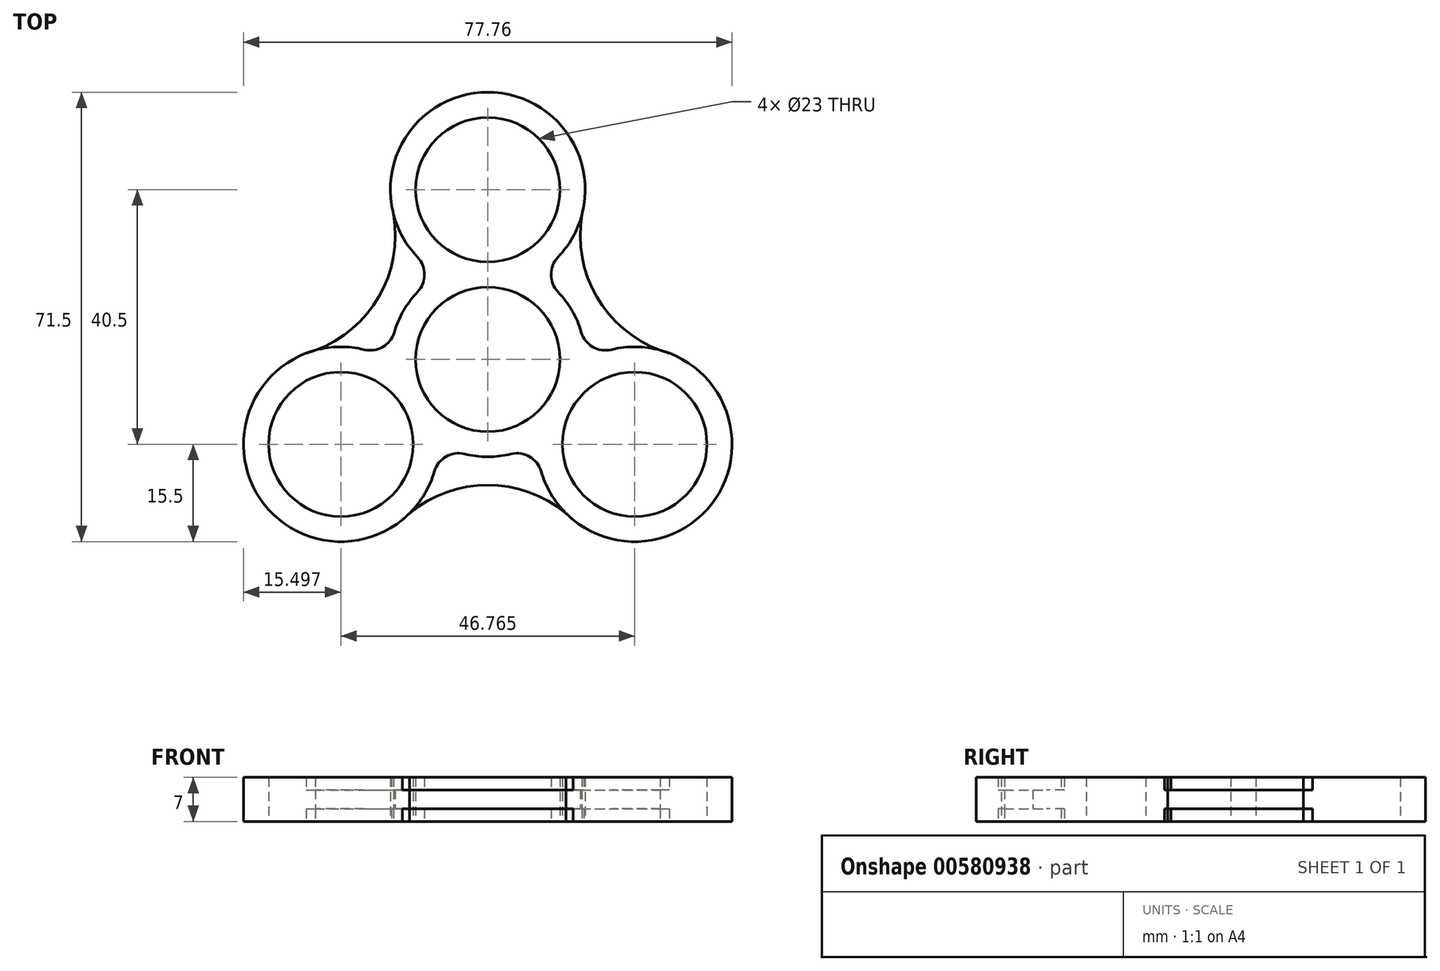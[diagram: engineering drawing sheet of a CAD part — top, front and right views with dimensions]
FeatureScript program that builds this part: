
annotation { "Feature Type Name" : "Feature", "Feature Type Description" : "" }
export const myFeature = defineFeature(function(context is Context, id is Id, definition is map)
    precondition{}
    {
        {
            var Q0;
            Q0=qCreatedBy(makeId("Top.planeOp"),FACE);
            var sketch = newSketch(context, id + "F0", { "sketchPlane" : qUnion([Q0])});
            skCircle(sketch, "E0", {"center": v(0, 0) * mm, "radius": 11.5 * mm});
            skLineSegment(sketch, "E1", {"start": v(0, 0) * mm, "end": v(0, 27) * mm});
            skCircle(sketch, "E2", {"center": v(0, 27) * mm, "radius": 11.5 * mm});
            skArc(sketch, "E3.0", {"start": v(11.18, 16.27) * mm, "mid": v(0, 42.5) * mm, "end": v(-11.18, 16.27) * mm});
            skCircle(sketch, "E4.1.0", {"center": v(-23.38, -13.5) * mm, "radius": 11.5 * mm});
            skArc(sketch, "E4.1.1", {"start": v(-19.68, 1.55) * mm, "mid": v(-36.8, -21.25) * mm, "end": v(-8.5, -17.82) * mm});
            skCircle(sketch, "E4.2.0", {"center": v(23.38, -13.5) * mm, "radius": 11.5 * mm});
            skArc(sketch, "E4.2.1", {"start": v(8.5, -17.82) * mm, "mid": v(36.8, -21.25) * mm, "end": v(19.68, 1.55) * mm});
            skArc(sketch, "E5", {"start": v(15.3, 24.5) * mm, "mid": v(17.31, 10) * mm, "end": v(28.87, 1) * mm});
            skArc(sketch, "E6.0", {"start": v(-11.18, 10.73) * mm, "mid": v(-13.42, 7.75) * mm, "end": v(-14.89, 4.32) * mm});
            skArc(sketch, "E7.trimOffspring", {"start": v(14.89, 4.32) * mm, "mid": v(13.42, 7.75) * mm, "end": v(11.18, 10.73) * mm});
            skArc(sketch, "E8.trimOffspring", {"start": v(-3.7, -15.05) * mm, "mid": v(0, -15.5) * mm, "end": v(3.7, -15.05) * mm});
            skPoint(sketch, "E9.visualSharp", {"position": v(7.62, 13.5) * mm});
            skArc(sketch, "E9.filletArc", {"start": v(11.18, 16.27) * mm, "mid": v(10.07, 13.5) * mm, "end": v(11.18, 10.73) * mm});
            skPoint(sketch, "E10.visualSharp", {"position": v(15.5, -0.15) * mm});
            skArc(sketch, "E10.filletArc", {"start": v(14.89, 4.32) * mm, "mid": v(16.73, 1.97) * mm, "end": v(19.68, 1.55) * mm});
            skPoint(sketch, "E11.visualSharp", {"position": v(7.88, -13.35) * mm});
            skArc(sketch, "E11.filletArc", {"start": v(8.5, -17.82) * mm, "mid": v(6.66, -15.47) * mm, "end": v(3.7, -15.05) * mm});
            skPoint(sketch, "E12.visualSharp", {"position": v(-7.88, -13.35) * mm});
            skArc(sketch, "E12.filletArc", {"start": v(-3.7, -15.05) * mm, "mid": v(-6.66, -15.47) * mm, "end": v(-8.5, -17.82) * mm});
            skPoint(sketch, "E13.visualSharp", {"position": v(-15.5, -0.15) * mm});
            skArc(sketch, "E13.filletArc", {"start": v(-19.68, 1.55) * mm, "mid": v(-16.73, 1.97) * mm, "end": v(-14.89, 4.32) * mm});
            skPoint(sketch, "E14.visualSharp", {"position": v(-7.62, 13.5) * mm});
            skArc(sketch, "E14.filletArc", {"start": v(-11.18, 10.73) * mm, "mid": v(-10.07, 13.5) * mm, "end": v(-11.18, 16.27) * mm});
            skArc(sketch, "E15.1.0", {"start": v(-28.87, 1) * mm, "mid": v(-17.31, 10) * mm, "end": v(-15.3, 24.5) * mm});
            skArc(sketch, "E15.2.0", {"start": v(13.57, -25.5) * mm, "mid": v(0, -20) * mm, "end": v(-13.57, -25.5) * mm});
            skSolve(sketch);
        }
        {
            var Q0;
            Q0=makeQuery(id+"F0.imprint","IMPRINT",FACE,{"disambiguationData":[TD([[makeQuery(id+"F0.imprint","IMPRINT",EDGE,{"derivedFrom":sQuery(id+"F0.wireOp",EDGE,"E0")}),-1.0]])]});
            extrude(context, id + "F1", {"entities" : qUnion([Q0]), "endBound" : BoundingType.SYMMETRIC, "depth" : 7 * mm, "offsetDistance" : 25 * mm});
        }
        {
            var Q0;
            {var subQ0=sQuery(id+"F0.wireOp",EDGE,"E5");var subQ1=sQuery(id+"F0.wireOp",EDGE,"E3.0");var subQ2=makeQuery(id+"F0.imprint","INTERSECT",VERTEX,{"disambiguationData":[OD(0.0)],"derivedFrom":[subQ1,subQ0]});Q0=makeQuery(id+"F0.imprint","IMPRINT",FACE,{"disambiguationData":[TD([[makeQuery(id+"F0.imprint","IMPRINT",EDGE,{"disambiguationData":[TD([[subQ2,1.0]])],"derivedFrom":subQ1}),1.0]])]});}
            var Q1;
            {var subQ0=sQuery(id+"F0.wireOp",EDGE,"E15.1.0");var subQ1=sQuery(id+"F0.wireOp",EDGE,"E3.0");var subQ2=makeQuery(id+"F0.imprint","INTERSECT",VERTEX,{"disambiguationData":[OD(0.0)],"derivedFrom":[subQ1,subQ0]});Q1=makeQuery(id+"F0.imprint","IMPRINT",FACE,{"disambiguationData":[TD([[makeQuery(id+"F0.imprint","IMPRINT",EDGE,{"disambiguationData":[TD([[subQ2,-1.0]])],"derivedFrom":subQ1}),1.0]])]});}
            var Q2;
            {var subQ0=sQuery(id+"F0.wireOp",EDGE,"E15.1.0");var subQ1=sQuery(id+"F0.wireOp",EDGE,"E4.1.1");var subQ2=makeQuery(id+"F0.imprint","INTERSECT",VERTEX,{"disambiguationData":[OD(0.0)],"derivedFrom":[subQ1,subQ0]});Q2=makeQuery(id+"F0.imprint","IMPRINT",FACE,{"disambiguationData":[TD([[makeQuery(id+"F0.imprint","IMPRINT",EDGE,{"disambiguationData":[TD([[subQ2,1.0]])],"derivedFrom":subQ1}),1.0]])]});}
            var Q3;
            {var subQ0=sQuery(id+"F0.wireOp",EDGE,"E15.2.0");var subQ1=sQuery(id+"F0.wireOp",EDGE,"E4.1.1");var subQ2=makeQuery(id+"F0.imprint","INTERSECT",VERTEX,{"disambiguationData":[OD(0.0)],"derivedFrom":[subQ1,subQ0]});Q3=makeQuery(id+"F0.imprint","IMPRINT",FACE,{"disambiguationData":[TD([[makeQuery(id+"F0.imprint","IMPRINT",EDGE,{"disambiguationData":[TD([[subQ2,-1.0]])],"derivedFrom":subQ1}),1.0]])]});}
            var Q4;
            {var subQ0=sQuery(id+"F0.wireOp",EDGE,"E15.2.0");var subQ1=sQuery(id+"F0.wireOp",EDGE,"E4.2.1");var subQ2=makeQuery(id+"F0.imprint","INTERSECT",VERTEX,{"disambiguationData":[OD(0.0)],"derivedFrom":[subQ1,subQ0]});Q4=makeQuery(id+"F0.imprint","IMPRINT",FACE,{"disambiguationData":[TD([[makeQuery(id+"F0.imprint","IMPRINT",EDGE,{"disambiguationData":[TD([[subQ2,1.0]])],"derivedFrom":subQ1}),1.0]])]});}
            var Q5;
            {var subQ0=sQuery(id+"F0.wireOp",EDGE,"E5");var subQ1=sQuery(id+"F0.wireOp",EDGE,"E4.2.1");var subQ2=makeQuery(id+"F0.imprint","INTERSECT",VERTEX,{"disambiguationData":[OD(0.0)],"derivedFrom":[subQ1,subQ0]});Q5=makeQuery(id+"F0.imprint","IMPRINT",FACE,{"disambiguationData":[TD([[makeQuery(id+"F0.imprint","IMPRINT",EDGE,{"disambiguationData":[TD([[subQ2,-1.0]])],"derivedFrom":subQ1}),1.0]])]});}
            var Q6;
            Q6=makeQuery(id+"F0.imprint","IMPRINT",FACE,{"disambiguationData":[TD([[makeQuery(id+"F0.imprint","IMPRINT",EDGE,{"derivedFrom":sQuery(id+"F0.wireOp",EDGE,"E0")}),-1.0]])]});
            var Q7;
            Q7=makeQuery(id+"F0.imprint","IMPRINT",FACE,{"disambiguationData":[TD([[makeQuery(id+"F0.imprint","IMPRINT",EDGE,{"derivedFrom":sQuery(id+"F0.wireOp",EDGE,"E6.0")}),-1.0]])]});
            var Q8;
            Q8=makeQuery(id+"F0.imprint","IMPRINT",FACE,{"disambiguationData":[TD([[makeQuery(id+"F0.imprint","IMPRINT",EDGE,{"derivedFrom":sQuery(id+"F0.wireOp",EDGE,"E8.trimOffspring")}),-1.0]])]});
            var Q9;
            Q9=makeQuery(id+"F0.imprint","IMPRINT",FACE,{"disambiguationData":[TD([[makeQuery(id+"F0.imprint","IMPRINT",EDGE,{"derivedFrom":sQuery(id+"F0.wireOp",EDGE,"E7.trimOffspring")}),-1.0]])]});
            extrude(context, id + "F2", {"entities" : qUnion([Q0, Q1, Q2, Q3, Q4, Q5, Q6, Q7, Q8, Q9]), "operationType" : NewBodyOperationType.ADD, "endBound" : BoundingType.SYMMETRIC, "depth" : 3 * mm, "offsetDistance" : 25 * mm});
        }
    });
